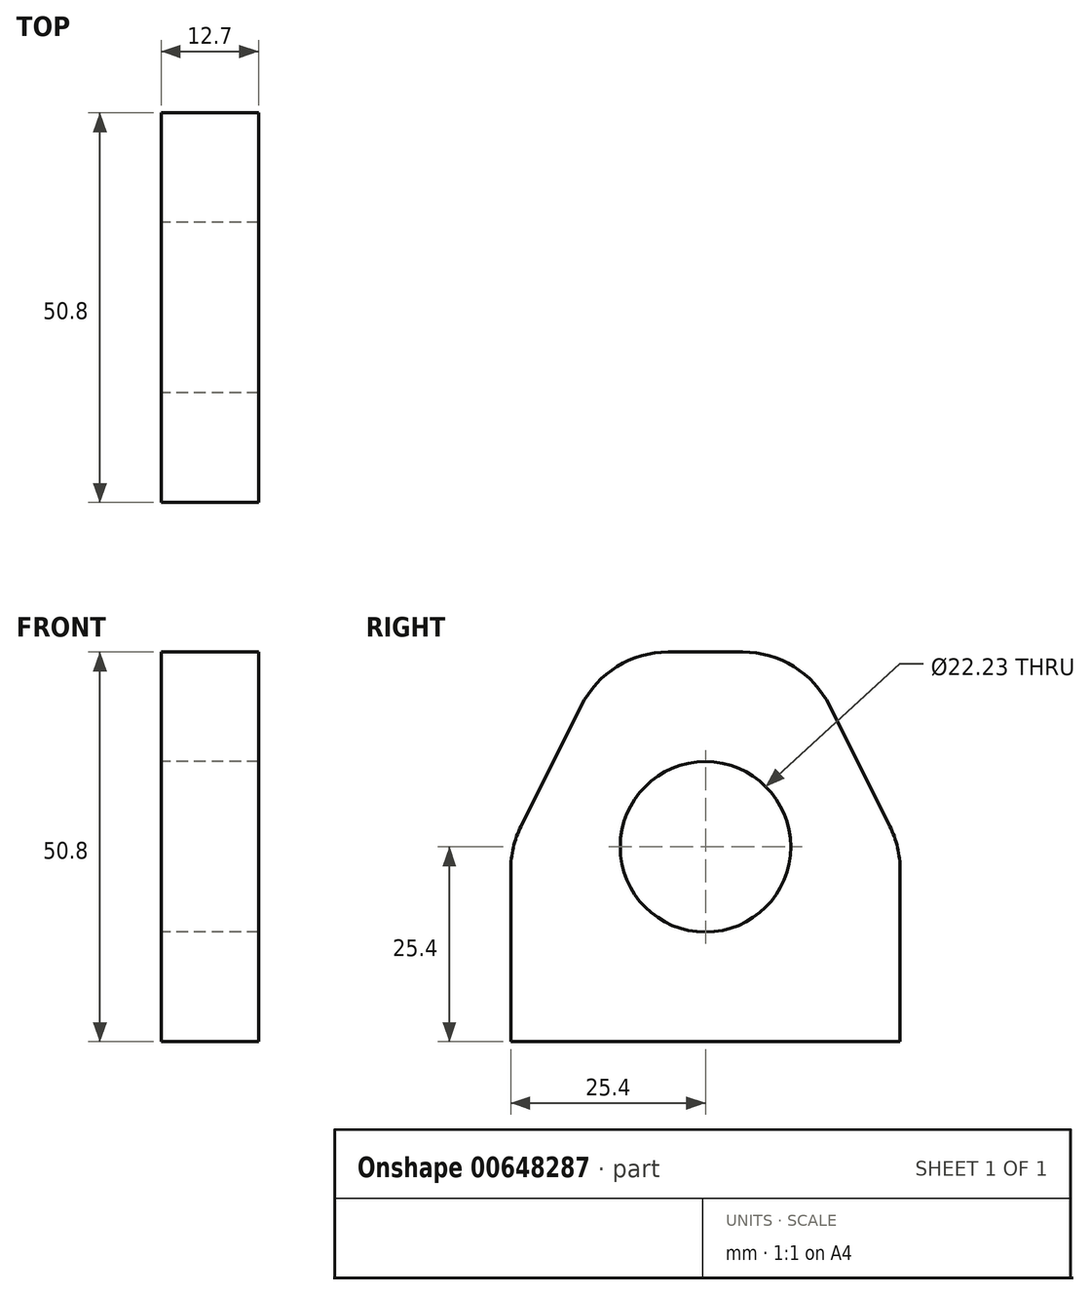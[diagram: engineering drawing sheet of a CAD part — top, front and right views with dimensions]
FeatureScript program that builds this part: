
annotation { "Feature Type Name" : "Feature", "Feature Type Description" : "" }
export const myFeature = defineFeature(function(context is Context, id is Id, definition is map)
    precondition{}
    {
        {
            var Q0;
            Q0=qCreatedBy(makeId("Right.planeOp"),FACE);
            var sketch = newSketch(context, id + "F0", { "sketchPlane" : qUnion([Q0])});
            skLineSegment(sketch, "E0", {"start": v(0, 25.4) * mm, "end": v(-4.85, 25.4) * mm});
            skLineSegment(sketch, "E1", {"start": v(-16.21, 18.38) * mm, "end": v(-24.06, 2.68) * mm});
            skLineSegment(sketch, "E2", {"start": v(-25.4, -3) * mm, "end": v(-25.4, -25.4) * mm});
            skLineSegment(sketch, "E3", {"start": v(-25.4, -25.4) * mm, "end": v(0, -25.4) * mm});
            skLineSegment(sketch, "E4", {"start": v(0, 25.4) * mm, "end": v(0, -25.4) * mm, "construction": true});
            skLineSegment(sketch, "E5.MirrorCS", {"start": v(25.4, -25.4) * mm, "end": v(0, -25.4) * mm});
            skLineSegment(sketch, "E6.MirrorCS", {"start": v(16.21, 18.38) * mm, "end": v(24.06, 2.68) * mm});
            skLineSegment(sketch, "E7.MirrorCS", {"start": v(25.4, -3) * mm, "end": v(25.4, -25.4) * mm});
            skLineSegment(sketch, "E8.MirrorCS", {"start": v(0, 25.4) * mm, "end": v(4.85, 25.4) * mm});
            skCircle(sketch, "E9", {"center": v(0, 0) * mm, "radius": 11.11 * mm});
            skPoint(sketch, "E10.visualSharp", {"position": v(-25.4, 0) * mm});
            skArc(sketch, "E10.filletArc", {"start": v(-24.06, 2.68) * mm, "mid": v(-25.06, -0.08) * mm, "end": v(-25.4, -3) * mm});
            skPoint(sketch, "E11.visualSharp", {"position": v(-12.7, 25.4) * mm});
            skArc(sketch, "E11.filletArc", {"start": v(-4.85, 25.4) * mm, "mid": v(-11.53, 23.5) * mm, "end": v(-16.21, 18.38) * mm});
            skPoint(sketch, "E12.visualSharp", {"position": v(12.7, 25.4) * mm});
            skArc(sketch, "E12.filletArc", {"start": v(16.21, 18.38) * mm, "mid": v(11.53, 23.5) * mm, "end": v(4.85, 25.4) * mm});
            skPoint(sketch, "E13.visualSharp", {"position": v(25.4, 0) * mm});
            skArc(sketch, "E13.filletArc", {"start": v(25.4, -3) * mm, "mid": v(25.06, -0.08) * mm, "end": v(24.06, 2.68) * mm});
            skSolve(sketch);
        }
        {
            var Q0;
            Q0=makeQuery(id+"F0.imprint","IMPRINT",FACE,{"disambiguationData":[TD([[makeQuery(id+"F0.imprint","IMPRINT",EDGE,{"derivedFrom":sQuery(id+"F0.wireOp",EDGE,"E0")}),1.0]])]});
            extrude(context, id + "F1", {"entities" : qUnion([Q0]), "depth" : 12.7 * mm, "offsetDistance" : 25.4 * mm});
        }
    });
